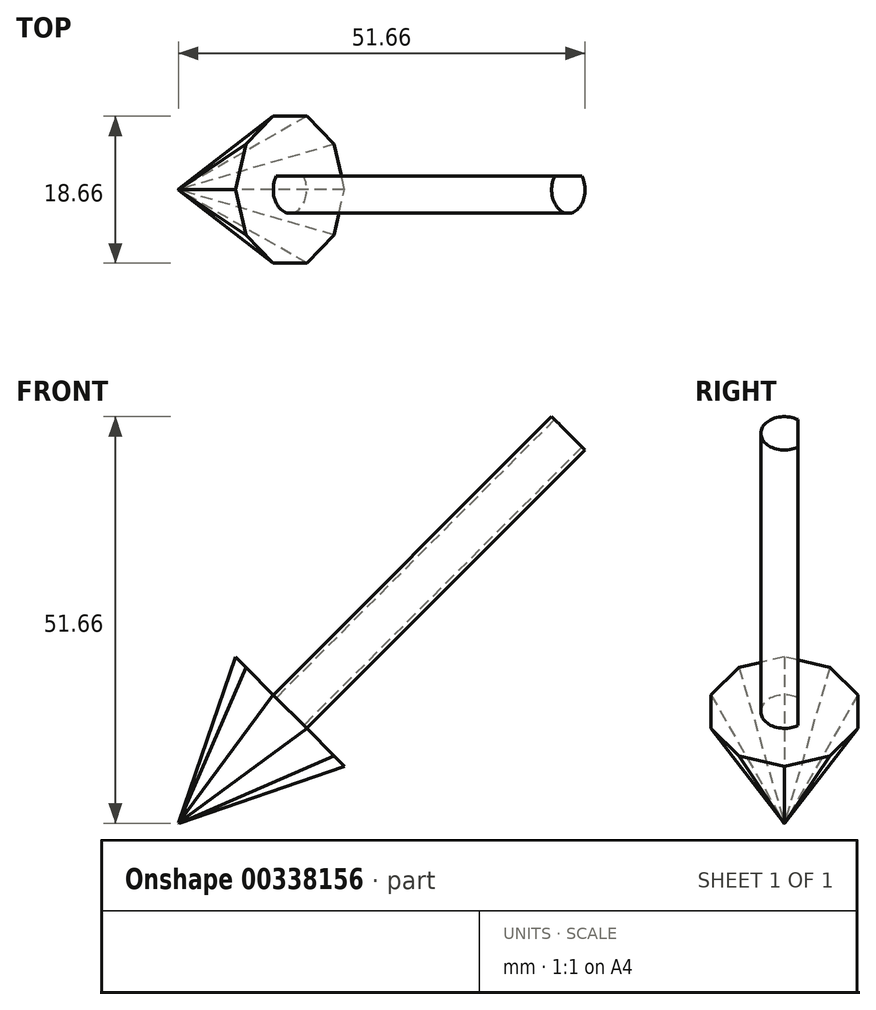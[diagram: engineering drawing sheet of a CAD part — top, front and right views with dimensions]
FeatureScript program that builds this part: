
annotation { "Feature Type Name" : "Feature", "Feature Type Description" : "" }
export const myFeature = defineFeature(function(context is Context, id is Id, definition is map)
    precondition{}
    {
        {
            var Q0;
            Q0=qCreatedBy(makeId("Front.planeOp"),FACE);
            var sketch = newSketch(context, id + "F0", { "sketchPlane" : qUnion([Q0])});
            skLineSegment(sketch, "E0", {"start": v(0, 0) * mm, "end": v(14.14, 14.14) * mm});
            skLineSegment(sketch, "E1", {"start": v(0, 0) * mm, "end": v(14.14, 0) * mm});
            skLineSegment(sketch, "E2", {"start": v(14.14, 14.14) * mm, "end": v(24.75, 3.54) * mm});
            skLineSegment(sketch, "E3", {"start": v(0, 0) * mm, "end": v(20.74, 7.55) * mm, "construction": true});
            skLineSegment(sketch, "E4", {"start": v(14.14, 14.14) * mm, "end": v(14.14, 8.83) * mm, "construction": true});
            skSolve(sketch);
        }
        {
            var Q0;
            Q0=sQuery(id+"F0.wireOp",EDGE,"E2");
            var Q1;
            Q1=qCreatedBy(makeId("Right.planeOp"),FACE);
            cPlane(context, id + "F1", {"entities" : qUnion([Q0, Q1]), "cplaneType" : CPlaneType.LINE_ANGLE, "offset" : 25 * mm, "angle" : 0 * degree, "width" : 150 * mm, "height" : 150 * mm});
        }
        {
            var Q0;
            Q0=qCreatedBy(id+"F1.planeOp",FACE);
            var sketch = newSketch(context, id + "F2", { "sketchPlane" : qUnion([Q0])});
            skCircle(sketch, "E5.cCircle", {"center": v(0, 0) * mm, "radius": 9.33 * mm, "construction": true});
            skLineSegment(sketch, "E5.0", {"start": v(-9.33, -3.03) * mm, "end": v(-9.33, 3.03) * mm});
            skLineSegment(sketch, "E5.1", {"start": v(-9.33, 3.03) * mm, "end": v(-5.76, 7.93) * mm});
            skLineSegment(sketch, "E5.2", {"start": v(-5.76, 7.93) * mm, "end": v(0, 9.8) * mm});
            skLineSegment(sketch, "E5.3", {"start": v(0, 9.8) * mm, "end": v(5.76, 7.93) * mm});
            skLineSegment(sketch, "E5.4", {"start": v(5.76, 7.93) * mm, "end": v(9.33, 3.03) * mm});
            skLineSegment(sketch, "E5.5", {"start": v(9.33, 3.03) * mm, "end": v(9.33, -3.03) * mm});
            skLineSegment(sketch, "E5.6", {"start": v(9.33, -3.03) * mm, "end": v(5.76, -7.93) * mm});
            skLineSegment(sketch, "E5.7", {"start": v(5.76, -7.93) * mm, "end": v(0, -9.8) * mm});
            skLineSegment(sketch, "E5.8", {"start": v(0, -9.8) * mm, "end": v(-5.76, -7.93) * mm});
            skLineSegment(sketch, "E5.9", {"start": v(-5.76, -7.93) * mm, "end": v(-9.33, -3.03) * mm});
            skPoint(sketch, "E5.0.midPoint", {"position": v(-9.33, 0) * mm});
            skPoint(sketch, "E6", {"position": v(9.33, 0) * mm});
            skSolve(sketch);
        }
        {
            var Q0;
            Q0=qCreatedBy(id+"F1.planeOp",FACE);
            var Q1;
            Q1=sQuery(id+"F0.wireOp",VERTEX,"E0.start");
            cPlane(context, id + "F3", {"entities" : qUnion([Q0, Q1]), "cplaneType" : CPlaneType.PLANE_POINT, "offset" : 25 * mm, "width" : 150 * mm, "height" : 150 * mm});
        }
        {
            var Q0;
            Q0=qCreatedBy(id+"F3.planeOp",FACE);
            var sketch = newSketch(context, id + "F4", { "sketchPlane" : qUnion([Q0])});
            skCircle(sketch, "E7.cCircle", {"center": v(0, 0) * mm, "radius": 0.05 * mm, "construction": true});
            skLineSegment(sketch, "E7.0", {"start": v(-0.05, -0.02) * mm, "end": v(-0.05, 0.02) * mm});
            skLineSegment(sketch, "E7.1", {"start": v(-0.05, 0.02) * mm, "end": v(-0.03, 0.04) * mm});
            skLineSegment(sketch, "E7.2", {"start": v(-0.03, 0.04) * mm, "end": v(0, 0.05) * mm});
            skLineSegment(sketch, "E7.3", {"start": v(0, 0.05) * mm, "end": v(0.03, 0.04) * mm});
            skLineSegment(sketch, "E7.4", {"start": v(0.03, 0.04) * mm, "end": v(0.05, 0.02) * mm});
            skLineSegment(sketch, "E7.5", {"start": v(0.05, 0.02) * mm, "end": v(0.05, -0.02) * mm});
            skLineSegment(sketch, "E7.6", {"start": v(0.05, -0.02) * mm, "end": v(0.03, -0.04) * mm});
            skLineSegment(sketch, "E7.7", {"start": v(0.03, -0.04) * mm, "end": v(0, -0.05) * mm});
            skLineSegment(sketch, "E7.8", {"start": v(0, -0.05) * mm, "end": v(-0.03, -0.04) * mm});
            skLineSegment(sketch, "E7.9", {"start": v(-0.03, -0.04) * mm, "end": v(-0.05, -0.02) * mm});
            skPoint(sketch, "E7.0.midPoint", {"position": v(-0.05, 0) * mm});
            skSolve(sketch);
        }
        {
            var Q0;
            Q0=makeQuery(id+"F2.imprint","IMPRINT",FACE,{"disambiguationData":[TD([[makeQuery(id+"F2.imprint","IMPRINT",EDGE,{"derivedFrom":sQuery(id+"F2.wireOp",EDGE,"E5.0")}),-1.0]])]});
            var Q1;
            Q1=makeQuery(id+"F4.imprint","IMPRINT",FACE,{"disambiguationData":[TD([[makeQuery(id+"F4.imprint","IMPRINT",EDGE,{"derivedFrom":sQuery(id+"F4.wireOp",EDGE,"E7.0")}),-1.0]])]});
            loft(context, id + "F5", {"sheetProfilesArray" : [{ "sheetProfileEntities" : qUnion([Q0]) }, { "sheetProfileEntities" : qUnion([Q1]) }]});
        }
        {
            var Q0;
            Q0=makeQuery(id+"F5.opLoft","CAP_FACE",FACE,{"disambiguationData":[OSD([makeQuery(id+"F2.imprint","IMPRINT",FACE,{"disambiguationData":[TD([[makeQuery(id+"F2.imprint","IMPRINT",EDGE,{"derivedFrom":sQuery(id+"F2.wireOp",EDGE,"E5.0")}),-1.0]])]})])],"isStart":true});
            var sketch = newSketch(context, id + "F6", { "sketchPlane" : qUnion([Q0])});
            skCircle(sketch, "E8", {"center": v(0, 0) * mm, "radius": 3 * mm});
            skLineSegment(sketch, "E9", {"start": v(1.7, -2.47) * mm, "end": v(1.7, 2.47) * mm});
            skSolve(sketch);
        }
        {
            var Q0;
            {var subQ0=sQuery(id+"F6.wireOp",EDGE,"E9");Q0=makeQuery(id+"F6.imprint","IMPRINT",FACE,{"disambiguationData":[TD([[makeQuery(id+"F6.imprint","IMPRINT",EDGE,{"derivedFrom":subQ0}),1.0]])]});}
            extrude(context, id + "F7", {"entities" : qUnion([Q0]), "operationType" : NewBodyOperationType.ADD, "depth" : 50 * mm});
        }
        {
            var Q0;
            Q0=qCreatedBy(makeId("Front.planeOp"),FACE);
            var sketch = newSketch(context, id + "F8", { "sketchPlane" : qUnion([Q0])});
            skLineSegment(sketch, "E10.bottom", {"start": v(8.84, 25.14) * mm, "end": v(13.84, 25.14) * mm});
            skLineSegment(sketch, "E10.top", {"start": v(8.84, 20.14) * mm, "end": v(13.84, 20.14) * mm});
            skLineSegment(sketch, "E10.left", {"start": v(8.84, 25.14) * mm, "end": v(8.84, 20.14) * mm});
            skLineSegment(sketch, "E10.right", {"start": v(13.84, 25.14) * mm, "end": v(13.84, 20.14) * mm});
            skSolve(sketch);
        }
        {
            var Q0;
            Q0=makeQuery(id+"F8.imprint","IMPRINT",FACE,{"disambiguationData":[TD([[makeQuery(id+"F8.imprint","IMPRINT",EDGE,{"derivedFrom":sQuery(id+"F8.wireOp",EDGE,"E10.bottom")}),-1.0]])]});
            extrude(context, id + "F9", {"entities" : qUnion([Q0]), "operationType" : NewBodyOperationType.REMOVE, "endBound" : BoundingType.SYMMETRIC, "depth" : 25 * mm});
        }
    });
